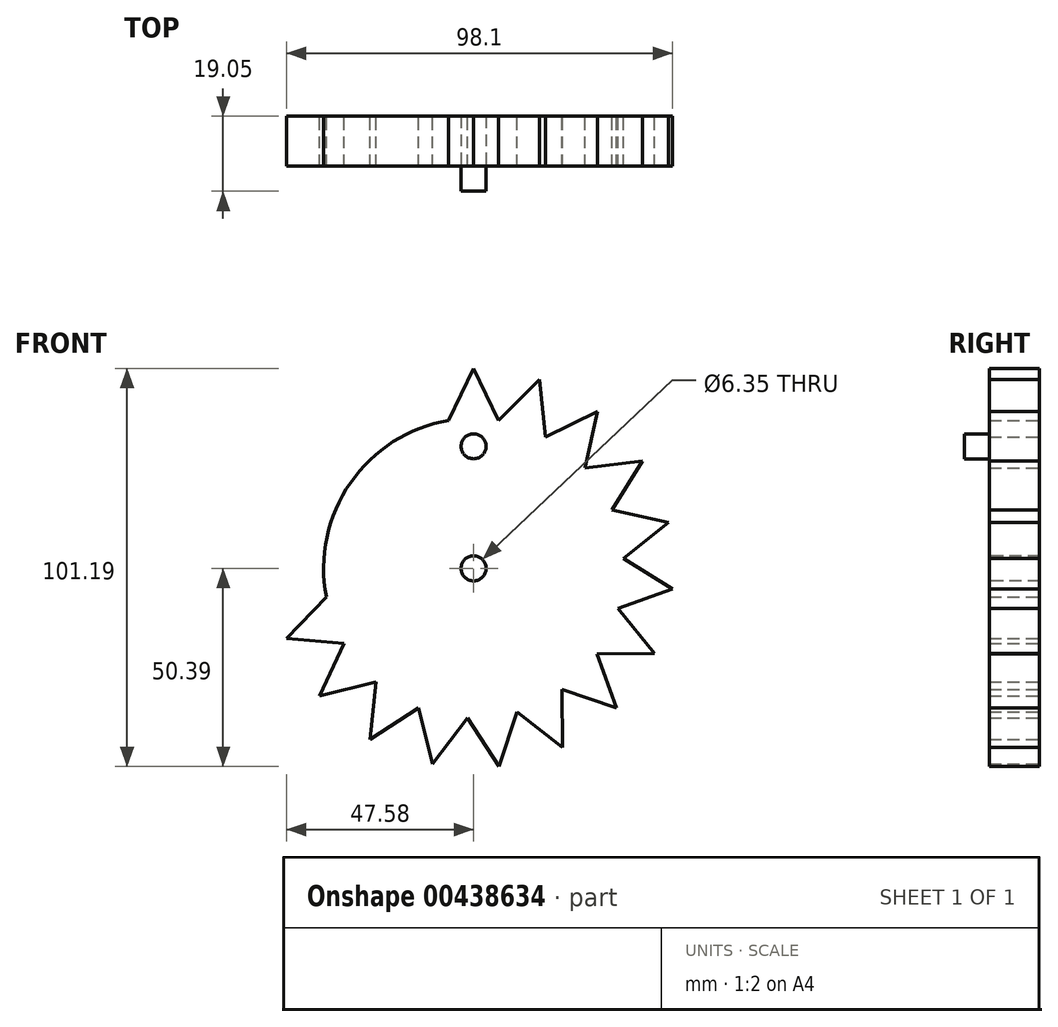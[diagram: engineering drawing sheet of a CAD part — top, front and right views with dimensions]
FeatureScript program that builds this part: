
annotation { "Feature Type Name" : "Feature", "Feature Type Description" : "" }
export const myFeature = defineFeature(function(context is Context, id is Id, definition is map)
    precondition{}
    {
        {
            var Q0;
            Q0=qCreatedBy(makeId("Front.planeOp"),FACE);
            var sketch = newSketch(context, id + "F0", { "sketchPlane" : qUnion([Q0])});
            skCircle(sketch, "E0", {"center": v(0, 0) * mm, "radius": 38.1 * mm});
            skPoint(sketch, "E1", {"position": v(0, 38.1) * mm});
            skPoint(sketch, "E2", {"position": v(12.52, 35.98) * mm});
            skPoint(sketch, "E3", {"position": v(23.65, 29.87) * mm});
            skPoint(sketch, "E4", {"position": v(32.16, 20.43) * mm});
            skPoint(sketch, "E5", {"position": v(37.09, 8.73) * mm});
            skPoint(sketch, "E6", {"position": v(37.9, -3.97) * mm});
            skPoint(sketch, "E7", {"position": v(34.48, -16.2) * mm});
            skPoint(sketch, "E8", {"position": v(27.24, -26.64) * mm});
            skPoint(sketch, "E9", {"position": v(16.97, -34.11) * mm});
            skPoint(sketch, "E10", {"position": v(4.82, -37.8) * mm});
            skPoint(sketch, "E11", {"position": v(-7.87, -37.28) * mm});
            skPoint(sketch, "E12", {"position": v(-19.68, -32.62) * mm});
            skPoint(sketch, "E13", {"position": v(-29.31, -24.34) * mm});
            skPoint(sketch, "E14", {"position": v(-35.68, -13.35) * mm});
            skLineSegment(sketch, "E15", {"start": v(0, 38.1) * mm, "end": v(0, 50.8) * mm});
            skLineSegment(sketch, "E16", {"start": v(0, 0) * mm, "end": v(12.52, 35.98) * mm});
            skLineSegment(sketch, "E17", {"start": v(0, 0) * mm, "end": v(23.65, 29.87) * mm});
            skLineSegment(sketch, "E18", {"start": v(0, 0) * mm, "end": v(32.16, 20.43) * mm});
            skLineSegment(sketch, "E19", {"start": v(0, 0) * mm, "end": v(37.09, 8.73) * mm});
            skLineSegment(sketch, "E20", {"start": v(0, 0) * mm, "end": v(37.9, -3.97) * mm});
            skLineSegment(sketch, "E21", {"start": v(0, 0) * mm, "end": v(34.48, -16.2) * mm});
            skLineSegment(sketch, "E22", {"start": v(0, 0) * mm, "end": v(27.24, -26.64) * mm});
            skLineSegment(sketch, "E23", {"start": v(0, 0) * mm, "end": v(16.97, -34.11) * mm});
            skLineSegment(sketch, "E24", {"start": v(0, 0) * mm, "end": v(4.82, -37.8) * mm});
            skLineSegment(sketch, "E25", {"start": v(0, 0) * mm, "end": v(-7.87, -37.28) * mm});
            skLineSegment(sketch, "E26", {"start": v(0, 0) * mm, "end": v(-19.68, -32.62) * mm});
            skLineSegment(sketch, "E27", {"start": v(0, 0) * mm, "end": v(-29.31, -24.34) * mm});
            skLineSegment(sketch, "E28", {"start": v(0, 0) * mm, "end": v(-35.68, -13.35) * mm});
            skLineSegment(sketch, "E29", {"start": v(12.52, 35.98) * mm, "end": v(16.7, 47.98) * mm});
            skLineSegment(sketch, "E30", {"start": v(23.65, 29.87) * mm, "end": v(31.54, 39.82) * mm});
            skLineSegment(sketch, "E31", {"start": v(32.16, 20.43) * mm, "end": v(42.87, 27.25) * mm});
            skLineSegment(sketch, "E32", {"start": v(37.09, 8.73) * mm, "end": v(49.45, 11.64) * mm});
            skLineSegment(sketch, "E33", {"start": v(34.48, -16.2) * mm, "end": v(45.98, -21.6) * mm});
            skLineSegment(sketch, "E34", {"start": v(27.24, -26.64) * mm, "end": v(36.32, -35.52) * mm});
            skLineSegment(sketch, "E35", {"start": v(16.97, -34.11) * mm, "end": v(22.63, -45.48) * mm});
            skLineSegment(sketch, "E36", {"start": v(4.82, -37.8) * mm, "end": v(6.43, -50.4) * mm});
            skLineSegment(sketch, "E37", {"start": v(-7.87, -37.28) * mm, "end": v(-10.5, -49.7) * mm});
            skLineSegment(sketch, "E38", {"start": v(-19.68, -32.62) * mm, "end": v(-26.25, -43.5) * mm});
            skLineSegment(sketch, "E39", {"start": v(-29.31, -24.34) * mm, "end": v(-39.08, -32.45) * mm});
            skLineSegment(sketch, "E40", {"start": v(-35.68, -13.35) * mm, "end": v(-47.58, -17.8) * mm});
            skLineSegment(sketch, "E41", {"start": v(37.9, -3.97) * mm, "end": v(50.52, -5.3) * mm});
            skPoint(sketch, "E42", {"position": v(-6.33, 37.57) * mm});
            skPoint(sketch, "E43", {"position": v(6.33, 37.57) * mm});
            skPoint(sketch, "E44", {"position": v(18.32, 33.4) * mm});
            skPoint(sketch, "E45", {"position": v(28.29, 25.53) * mm});
            skPoint(sketch, "E46", {"position": v(35.1, 14.81) * mm});
            skPoint(sketch, "E47", {"position": v(36.7, -10.2) * mm});
            skPoint(sketch, "E48", {"position": v(31.31, -21.7) * mm});
            skPoint(sketch, "E49", {"position": v(22.44, -30.8) * mm});
            skPoint(sketch, "E50", {"position": v(-1.52, -38.07) * mm});
            skPoint(sketch, "E51", {"position": v(-13.95, -35.45) * mm});
            skPoint(sketch, "E52", {"position": v(-24.83, -28.9) * mm});
            skPoint(sketch, "E53", {"position": v(-32.95, -19.13) * mm});
            skPoint(sketch, "E54", {"position": v(-37.4, -7.24) * mm});
            skPoint(sketch, "E55", {"position": v(38.02, 2.45) * mm});
            skPoint(sketch, "E56", {"position": v(11.07, -36.46) * mm});
            skLineSegment(sketch, "E57", {"start": v(-6.33, 37.57) * mm, "end": v(0, 50.8) * mm});
            skLineSegment(sketch, "E58", {"start": v(0, 50.8) * mm, "end": v(6.33, 37.57) * mm});
            skLineSegment(sketch, "E59", {"start": v(6.33, 37.57) * mm, "end": v(16.7, 47.98) * mm});
            skLineSegment(sketch, "E60", {"start": v(16.7, 47.98) * mm, "end": v(18.32, 33.4) * mm});
            skLineSegment(sketch, "E61", {"start": v(18.32, 33.4) * mm, "end": v(31.54, 39.82) * mm});
            skLineSegment(sketch, "E62", {"start": v(31.54, 39.82) * mm, "end": v(28.29, 25.53) * mm});
            skLineSegment(sketch, "E63", {"start": v(28.29, 25.53) * mm, "end": v(42.87, 27.25) * mm});
            skLineSegment(sketch, "E64", {"start": v(42.87, 27.25) * mm, "end": v(35.1, 14.81) * mm});
            skLineSegment(sketch, "E65", {"start": v(35.1, 14.81) * mm, "end": v(49.45, 11.64) * mm});
            skLineSegment(sketch, "E66", {"start": v(49.45, 11.64) * mm, "end": v(38.02, 2.45) * mm});
            skLineSegment(sketch, "E67", {"start": v(38.02, 2.45) * mm, "end": v(50.52, -5.3) * mm});
            skLineSegment(sketch, "E68", {"start": v(50.52, -5.3) * mm, "end": v(36.7, -10.2) * mm});
            skLineSegment(sketch, "E69", {"start": v(36.7, -10.2) * mm, "end": v(45.98, -21.6) * mm});
            skLineSegment(sketch, "E70", {"start": v(45.98, -21.6) * mm, "end": v(31.31, -21.7) * mm});
            skLineSegment(sketch, "E71", {"start": v(31.31, -21.7) * mm, "end": v(36.32, -35.52) * mm});
            skLineSegment(sketch, "E72", {"start": v(36.32, -35.52) * mm, "end": v(22.44, -30.8) * mm});
            skLineSegment(sketch, "E73", {"start": v(22.44, -30.8) * mm, "end": v(22.63, -45.48) * mm});
            skLineSegment(sketch, "E74", {"start": v(22.63, -45.48) * mm, "end": v(11.07, -36.46) * mm});
            skLineSegment(sketch, "E75", {"start": v(11.07, -36.46) * mm, "end": v(6.43, -50.4) * mm});
            skLineSegment(sketch, "E76", {"start": v(6.43, -50.4) * mm, "end": v(-1.52, -38.07) * mm});
            skLineSegment(sketch, "E77", {"start": v(-1.52, -38.07) * mm, "end": v(-10.5, -49.7) * mm});
            skLineSegment(sketch, "E78", {"start": v(-10.5, -49.7) * mm, "end": v(-13.95, -35.45) * mm});
            skLineSegment(sketch, "E79", {"start": v(-13.95, -35.45) * mm, "end": v(-26.25, -43.5) * mm});
            skLineSegment(sketch, "E80", {"start": v(-26.25, -43.5) * mm, "end": v(-24.83, -28.9) * mm});
            skLineSegment(sketch, "E81", {"start": v(-24.83, -28.9) * mm, "end": v(-39.08, -32.45) * mm});
            skLineSegment(sketch, "E82", {"start": v(-39.08, -32.45) * mm, "end": v(-32.95, -19.13) * mm});
            skLineSegment(sketch, "E83", {"start": v(-32.95, -19.13) * mm, "end": v(-47.58, -17.8) * mm});
            skLineSegment(sketch, "E84", {"start": v(-47.58, -17.8) * mm, "end": v(-37.4, -7.24) * mm});
            skSolve(sketch);
        }
        {
            var Q0;
            Q0 = qSketchRegion(id + "F0", true);
            extrude(context, id + "F1", {"entities" : qUnion([Q0]), "depth" : 12.7 * mm});
        }
        {
            var Q0;
            Q0=makeQuery(id+"F1.opExtrude","CAP_FACE",FACE,{"disambiguationData":[OSD([sQuery(id+"F0.wireOp",EDGE,"E0"),sQuery(id+"F0.wireOp",EDGE,"E57"),sQuery(id+"F0.wireOp",EDGE,"E58"),sQuery(id+"F0.wireOp",EDGE,"E59"),sQuery(id+"F0.wireOp",EDGE,"E60"),sQuery(id+"F0.wireOp",EDGE,"E61"),sQuery(id+"F0.wireOp",EDGE,"E62"),sQuery(id+"F0.wireOp",EDGE,"E63"),sQuery(id+"F0.wireOp",EDGE,"E64"),sQuery(id+"F0.wireOp",EDGE,"E65"),sQuery(id+"F0.wireOp",EDGE,"E66"),sQuery(id+"F0.wireOp",EDGE,"E67"),sQuery(id+"F0.wireOp",EDGE,"E68"),sQuery(id+"F0.wireOp",EDGE,"E69"),sQuery(id+"F0.wireOp",EDGE,"E70"),sQuery(id+"F0.wireOp",EDGE,"E71"),sQuery(id+"F0.wireOp",EDGE,"E72"),sQuery(id+"F0.wireOp",EDGE,"E73"),sQuery(id+"F0.wireOp",EDGE,"E74"),sQuery(id+"F0.wireOp",EDGE,"E75"),sQuery(id+"F0.wireOp",EDGE,"E76"),sQuery(id+"F0.wireOp",EDGE,"E77"),sQuery(id+"F0.wireOp",EDGE,"E78"),sQuery(id+"F0.wireOp",EDGE,"E79"),sQuery(id+"F0.wireOp",EDGE,"E80"),sQuery(id+"F0.wireOp",EDGE,"E81"),sQuery(id+"F0.wireOp",EDGE,"E82"),sQuery(id+"F0.wireOp",EDGE,"E83"),sQuery(id+"F0.wireOp",EDGE,"E84")])],"isStart":false});
            var sketch = newSketch(context, id + "F2", { "sketchPlane" : qUnion([Q0])});
            skCircle(sketch, "E85", {"center": v(0, 0) * mm, "radius": 3.18 * mm});
            skSolve(sketch);
        }
        {
            var Q0;
            Q0=makeQuery(id+"F2.imprint","IMPRINT",FACE,{"disambiguationData":[TD([[makeQuery(id+"F2.imprint","IMPRINT",EDGE,{"derivedFrom":sQuery(id+"F2.wireOp",EDGE,"E85")}),1.0]])]});
            extrude(context, id + "F3", {"entities" : qUnion([Q0]), "operationType" : NewBodyOperationType.REMOVE, "oppositeDirection" : true, "depth" : 25.4 * mm});
        }
        {
            var Q0;
            Q0=makeQuery(id+"F1.opExtrude","CAP_FACE",FACE,{"disambiguationData":[OSD([sQuery(id+"F0.wireOp",EDGE,"E0"),sQuery(id+"F0.wireOp",EDGE,"E57"),sQuery(id+"F0.wireOp",EDGE,"E58"),sQuery(id+"F0.wireOp",EDGE,"E59"),sQuery(id+"F0.wireOp",EDGE,"E60"),sQuery(id+"F0.wireOp",EDGE,"E61"),sQuery(id+"F0.wireOp",EDGE,"E62"),sQuery(id+"F0.wireOp",EDGE,"E63"),sQuery(id+"F0.wireOp",EDGE,"E64"),sQuery(id+"F0.wireOp",EDGE,"E65"),sQuery(id+"F0.wireOp",EDGE,"E66"),sQuery(id+"F0.wireOp",EDGE,"E67"),sQuery(id+"F0.wireOp",EDGE,"E68"),sQuery(id+"F0.wireOp",EDGE,"E69"),sQuery(id+"F0.wireOp",EDGE,"E70"),sQuery(id+"F0.wireOp",EDGE,"E71"),sQuery(id+"F0.wireOp",EDGE,"E72"),sQuery(id+"F0.wireOp",EDGE,"E73"),sQuery(id+"F0.wireOp",EDGE,"E74"),sQuery(id+"F0.wireOp",EDGE,"E75"),sQuery(id+"F0.wireOp",EDGE,"E76"),sQuery(id+"F0.wireOp",EDGE,"E77"),sQuery(id+"F0.wireOp",EDGE,"E78"),sQuery(id+"F0.wireOp",EDGE,"E79"),sQuery(id+"F0.wireOp",EDGE,"E80"),sQuery(id+"F0.wireOp",EDGE,"E81"),sQuery(id+"F0.wireOp",EDGE,"E82"),sQuery(id+"F0.wireOp",EDGE,"E83"),sQuery(id+"F0.wireOp",EDGE,"E84")])],"isStart":false});
            var sketch = newSketch(context, id + "F4", { "sketchPlane" : qUnion([Q0])});
            skPoint(sketch, "E86", {"position": v(0, 31) * mm});
            skCircle(sketch, "E87", {"center": v(0, 31) * mm, "radius": 3.18 * mm});
            skSolve(sketch);
        }
        {
            var Q0;
            Q0=makeQuery(id+"F4.imprint","IMPRINT",FACE,{"disambiguationData":[TD([[makeQuery(id+"F4.imprint","IMPRINT",EDGE,{"derivedFrom":sQuery(id+"F4.wireOp",EDGE,"E87")}),1.0]])]});
            extrude(context, id + "F5", {"entities" : qUnion([Q0]), "operationType" : NewBodyOperationType.ADD, "depth" : 6.35 * mm});
        }
    });
